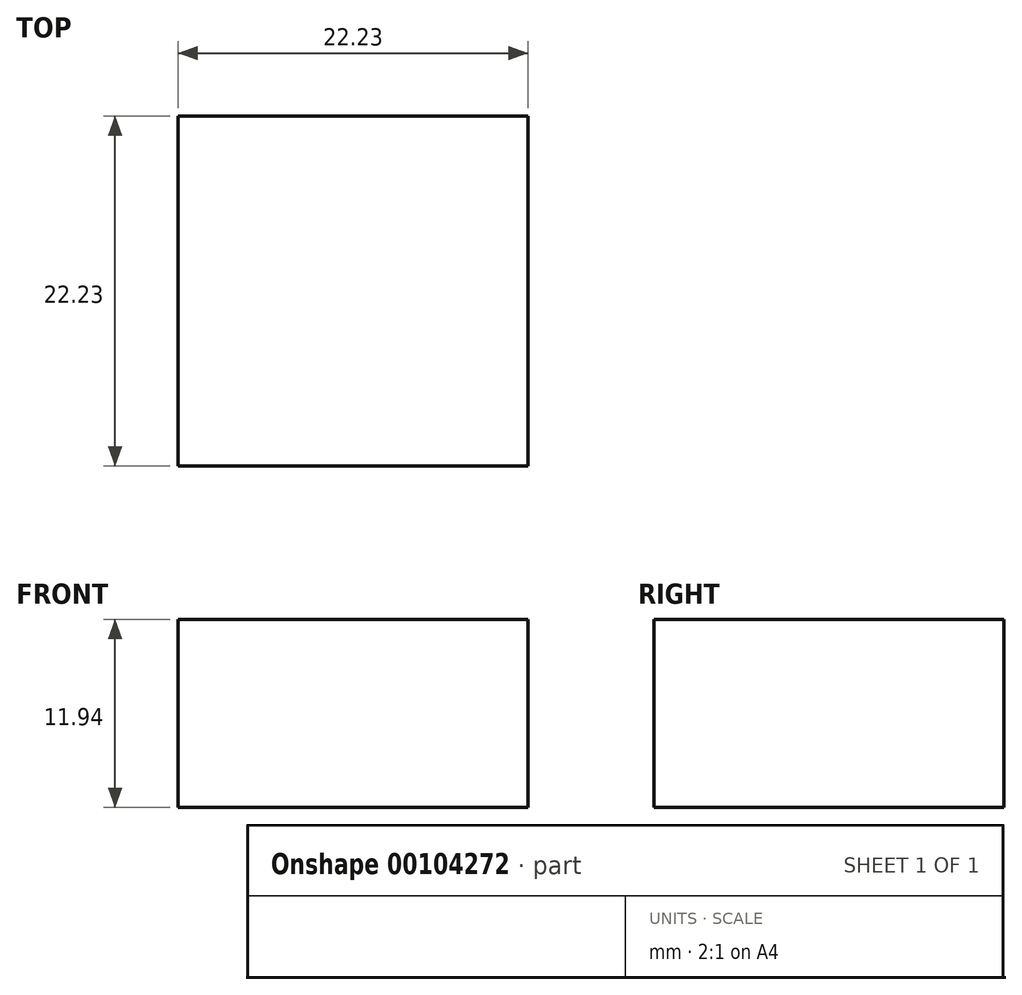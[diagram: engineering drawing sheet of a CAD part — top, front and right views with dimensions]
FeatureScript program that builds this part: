
annotation { "Feature Type Name" : "Feature", "Feature Type Description" : "" }
export const myFeature = defineFeature(function(context is Context, id is Id, definition is map)
    precondition{}
    {
        {
            var Q0;
            Q0=qCreatedBy(makeId("Top.planeOp"),FACE);
            var sketch = newSketch(context, id + "F0", { "sketchPlane" : qUnion([Q0])});
            skLineSegment(sketch, "E0.bottom", {"start": v(-10.37, 25.36) * mm, "end": v(11.86, 25.36) * mm});
            skLineSegment(sketch, "E0.top", {"start": v(-10.37, 3.13) * mm, "end": v(11.86, 3.13) * mm});
            skLineSegment(sketch, "E0.left", {"start": v(-10.37, 25.36) * mm, "end": v(-10.37, 3.13) * mm});
            skLineSegment(sketch, "E0.right", {"start": v(11.86, 25.36) * mm, "end": v(11.86, 3.13) * mm});
            skSolve(sketch);
        }
        {
            var Q0;
            Q0 = qSketchRegion(id + "F0", true);
            var Q1;
            Q1=makeQuery(id+"F0.imprint","IMPRINT",FACE,{"disambiguationData":[TD([[makeQuery(id+"F0.imprint","IMPRINT",EDGE,{"derivedFrom":sQuery(id+"F0.wireOp",EDGE,"E0.bottom")}),-1.0]])]});
            extrude(context, id + "F1", {"entities" : qUnion([Q0, Q1]), "depth" : 11.94 * mm});
        }
    });
